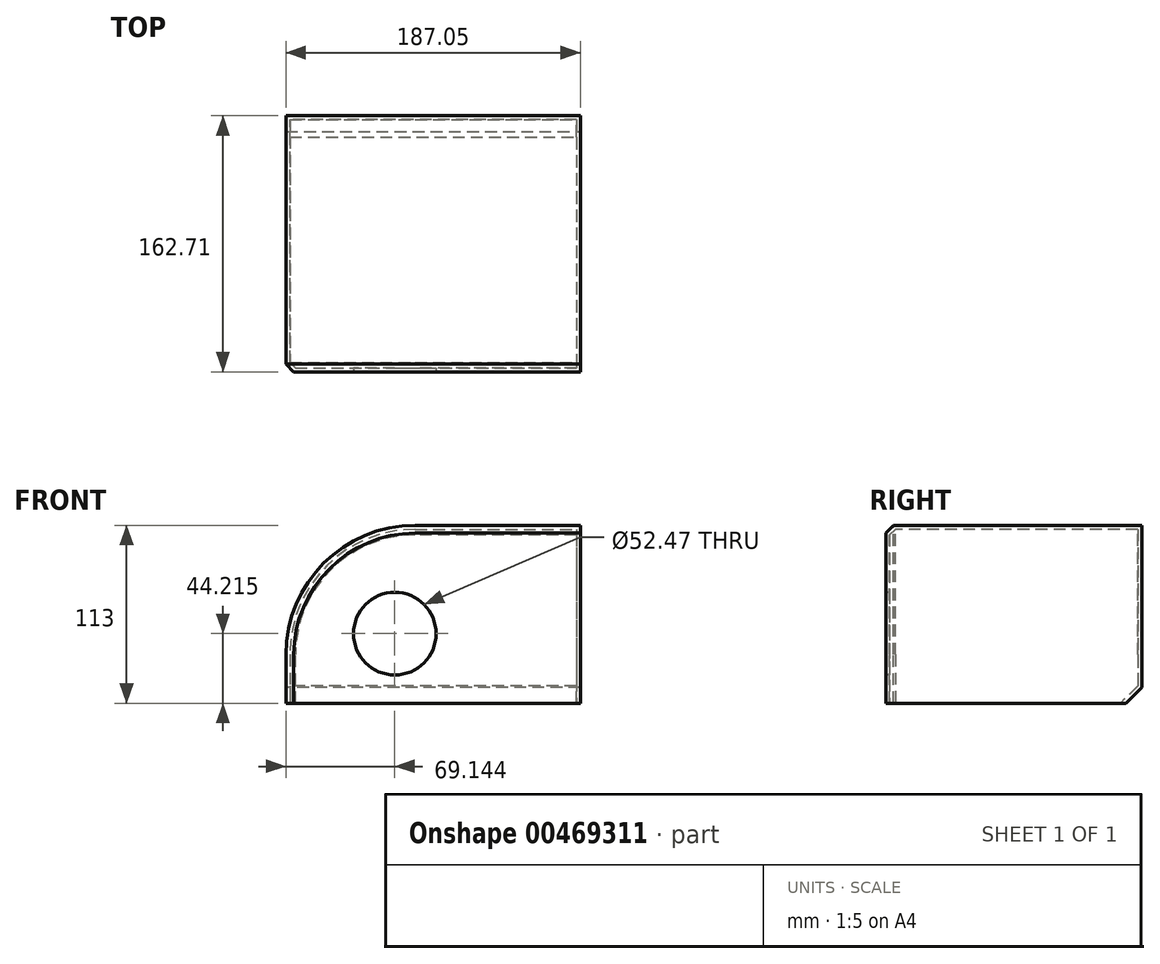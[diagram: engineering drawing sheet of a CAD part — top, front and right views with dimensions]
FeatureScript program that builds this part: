
annotation { "Feature Type Name" : "Feature", "Feature Type Description" : "" }
export const myFeature = defineFeature(function(context is Context, id is Id, definition is map)
    precondition{}
    {
        {
            var Q0;
            Q0=qCreatedBy(makeId("Top.planeOp"),FACE);
            var sketch = newSketch(context, id + "F0", { "sketchPlane" : qUnion([Q0])});
            skLineSegment(sketch, "E0.bottom", {"start": v(-93.71, 39.87) * mm, "end": v(93.34, 39.87) * mm});
            skLineSegment(sketch, "E0.top", {"start": v(-93.71, -122.84) * mm, "end": v(93.34, -122.84) * mm});
            skLineSegment(sketch, "E0.left", {"start": v(-93.71, 39.87) * mm, "end": v(-93.71, -122.84) * mm});
            skLineSegment(sketch, "E0.right", {"start": v(93.34, 39.87) * mm, "end": v(93.34, -122.84) * mm});
            skSolve(sketch);
        }
        {
            var Q0;
            Q0=makeQuery(id+"F0.imprint","IMPRINT",FACE,{"disambiguationData":[TD([[makeQuery(id+"F0.imprint","IMPRINT",EDGE,{"derivedFrom":sQuery(id+"F0.wireOp",EDGE,"E0.bottom")}),-1.0]])]});
            extrude(context, id + "F1", {"entities" : qUnion([Q0]), "depth" : 113 * mm});
        }
        {
            var Q0;
            Q0=makeQuery(id+"F1.opExtrude","CAP_EDGE",EDGE,{"disambiguationData":[OSD([sQuery(id+"F0.wireOp",EDGE,"E0.left")])],"isStart":false});
            fillet(context, id + "F2", {"entities" : qUnion([Q0]), "radius" : 82.08 * mm, "tangentPropagation" : true, "allowEdgeOverflow" : false});
        }
        {
            var Q0;
            Q0=makeQuery(id+"F1.opExtrude","CAP_EDGE",EDGE,{"disambiguationData":[OSD([sQuery(id+"F0.wireOp",EDGE,"E0.top")])],"isStart":false});
            chamfer(context, id + "F3", {"entities" : qUnion([Q0]), "width" : 5 * mm, "tangentPropagation" : true});
        }
        {
            var Q0;
            Q0=makeQuery(id+"F1.opExtrude","CAP_EDGE",EDGE,{"disambiguationData":[OSD([sQuery(id+"F0.wireOp",EDGE,"E0.bottom")])],"isStart":true});
            chamfer(context, id + "F4", {"entities" : qUnion([Q0]), "width" : 10 * mm, "tangentPropagation" : true});
        }
        {
            var Q0;
            Q0=makeQuery(id+"F1.opExtrude","CAP_FACE",FACE,{"disambiguationData":[OSD([sQuery(id+"F0.wireOp",EDGE,"E0.bottom"),sQuery(id+"F0.wireOp",EDGE,"E0.top"),sQuery(id+"F0.wireOp",EDGE,"E0.left"),sQuery(id+"F0.wireOp",EDGE,"E0.right")])],"isStart":true});
            shell(context, id + "F5", {"entities" : qUnion([Q0]), "thickness" : 2.5 * mm});
        }
        {
            var Q0;
            Q0=makeQuery(id+"F1.opExtrude","SWEPT_FACE",FACE,{"disambiguationData":[OSD([sQuery(id+"F0.wireOp",EDGE,"E0.top")])]});
            var sketch = newSketch(context, id + "F6", { "sketchPlane" : qUnion([Q0])});
            skCircle(sketch, "E1", {"center": v(-24.57, 44.22) * mm, "radius": 26.24 * mm});
            skSolve(sketch);
        }
        {
            var Q0;
            Q0=makeQuery(id+"F6.imprint","IMPRINT",FACE,{"disambiguationData":[TD([[makeQuery(id+"F6.imprint","IMPRINT",EDGE,{"derivedFrom":sQuery(id+"F6.wireOp",EDGE,"E1")}),1.0]])]});
            extrude(context, id + "F7", {"entities" : qUnion([Q0]), "operationType" : NewBodyOperationType.REMOVE, "oppositeDirection" : true, "depth" : 78 * mm});
        }
    });
